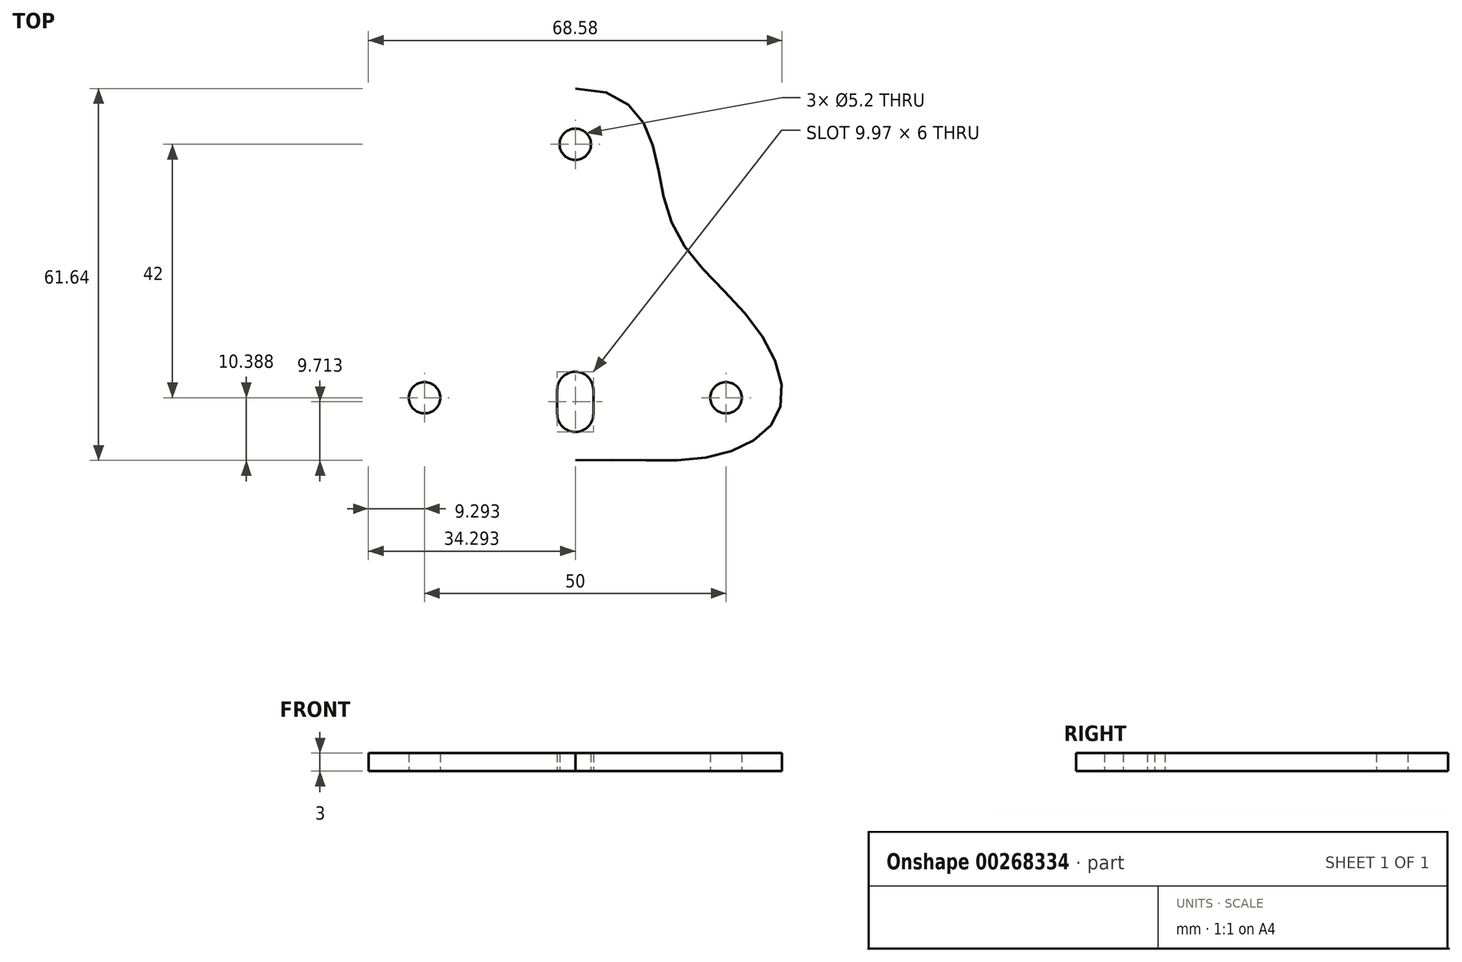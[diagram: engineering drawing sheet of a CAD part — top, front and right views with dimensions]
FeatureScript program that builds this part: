
annotation { "Feature Type Name" : "Feature", "Feature Type Description" : "" }
export const myFeature = defineFeature(function(context is Context, id is Id, definition is map)
    precondition{}
    {
        {
            var Q0;
            Q0=qCreatedBy(makeId("Top.planeOp"),FACE);
            var sketch = newSketch(context, id + "F0", { "sketchPlane" : qUnion([Q0])});
            skCircle(sketch, "E0", {"center": v(12.46, 4.43) * mm, "radius": 2.6 * mm});
            skCircle(sketch, "E1", {"center": v(37.46, -37.57) * mm, "radius": 2.6 * mm});
            skCircle(sketch, "E2", {"center": v(-12.54, -37.57) * mm, "radius": 2.6 * mm});
            skArc(sketch, "E3", {"start": v(9.46, -40.23) * mm, "mid": v(12.46, -43.23) * mm, "end": v(15.46, -40.23) * mm});
            skLineSegment(sketch, "E4", {"start": v(12.46, 5.9) * mm, "end": v(12.46, -52.9) * mm, "construction": true});
            skFitSpline(sketch, "E5", {"points": [v(12.46, 13.68) * mm, v(24.74, 5.9) * mm, v(29.06, -9.94) * mm, v(42.45, -25.92) * mm, v(46.34, -39.46) * mm, v(36.7, -46.95) * mm, v(12.46, -47.95) * mm], "startDerivative": vector(135.1, 3) * mm, "endDerivative": vector(-145.53, -5.3) * mm});
            skFitSpline(sketch, "E6.MirrorCS", {"points": [v(12.46, 13.68) * mm, v(0.18, 5.9) * mm, v(-4.14, -9.94) * mm, v(-17.53, -25.92) * mm, v(-21.42, -39.46) * mm, v(-11.77, -46.95) * mm, v(12.46, -47.95) * mm], "startDerivative": vector(-135.1, 3) * mm, "endDerivative": vector(145.53, -5.3) * mm});
            skLineSegment(sketch, "E7", {"start": v(9.46, -40.23) * mm, "end": v(9.46, -36.26) * mm});
            skLineSegment(sketch, "E8", {"start": v(15.46, -40.23) * mm, "end": v(15.46, -36.16) * mm});
            skArc(sketch, "E9", {"start": v(15.46, -36.16) * mm, "mid": v(12.41, -33.26) * mm, "end": v(9.46, -36.26) * mm});
            skSolve(sketch);
        }
        {
            var Q0;
            Q0=qSketchRegion(id+"F0",true);
            extrude(context, id + "F1", {"entities" : qUnion([Q0]), "depth" : 3 * mm});
        }
        {
            var Q0;
            Q0=makeQuery(id+"F1.opExtrude","CAP_FACE",FACE,{"disambiguationData":[OSD([sQuery(id+"F0.wireOp",EDGE,"E0"),sQuery(id+"F0.wireOp",EDGE,"E1"),sQuery(id+"F0.wireOp",EDGE,"E2"),sQuery(id+"F0.wireOp",EDGE,"E3"),sQuery(id+"F0.wireOp",EDGE,"gXV22Ezd-BxGV-p7MN-5mEq-ep9CFymhMpRn"),sQuery(id+"F0.wireOp",EDGE,"WmkqfEUB-IWB8-ESqq-jCjN-kpA6IxgFtCK6"),sQuery(id+"F0.wireOp",EDGE,"E5"),sQuery(id+"F0.wireOp",EDGE,"E6.MirrorCS")])],"isStart":false});
            var sketch = newSketch(context, id + "F2", { "sketchPlane" : qUnion([Q0])});
            skCircle(sketch, "E10", {"center": v(13.2, -12.8) * mm, "radius": 8.8 * mm});
            skCircle(sketch, "E11", {"center": v(2.84, -28.45) * mm, "radius": 6.03 * mm});
            skCircle(sketch, "E12", {"center": v(22.14, -29.31) * mm, "radius": 6.13 * mm});
            skSolve(sketch);
        }
    });
